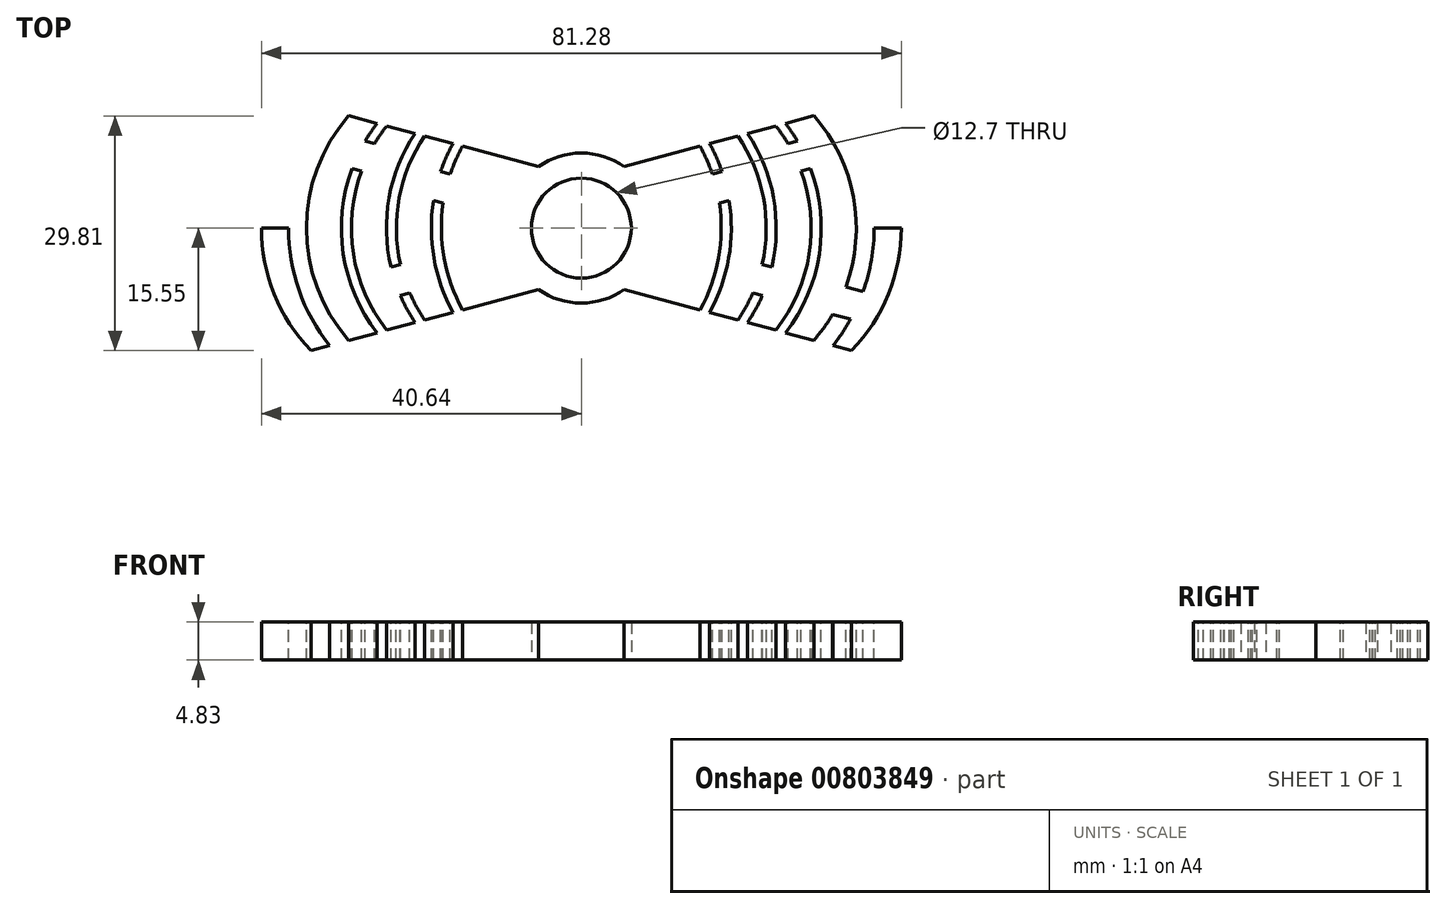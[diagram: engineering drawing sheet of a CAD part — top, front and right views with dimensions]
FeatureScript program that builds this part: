
annotation { "Feature Type Name" : "Feature", "Feature Type Description" : "" }
export const myFeature = defineFeature(function(context is Context, id is Id, definition is map)
    precondition{}
    {
        {
            var Q0;
            Q0=qCreatedBy(makeId("Top.planeOp"),FACE);
            var sketch = newSketch(context, id + "F0", { "sketchPlane" : qUnion([Q0])});
            skCircle(sketch, "E0", {"center": v(0, 0) * mm, "radius": 6.35 * mm});
            skCircle(sketch, "E1", {"center": v(0, 0) * mm, "radius": 9.53 * mm});
            skLineSegment(sketch, "E2", {"start": v(0, 0) * mm, "end": v(40.64, 0) * mm});
            skLineSegment(sketch, "E3", {"start": v(0, 0) * mm, "end": v(-40.64, 0) * mm});
            skLineSegment(sketch, "E4", {"start": v(0, 6.35) * mm, "end": v(34.35, 15.55) * mm});
            skLineSegment(sketch, "E5", {"start": v(0, -6.35) * mm, "end": v(34.35, -15.55) * mm});
            skLineSegment(sketch, "E6", {"start": v(0, -6.35) * mm, "end": v(-34.35, -15.55) * mm});
            skLineSegment(sketch, "E7", {"start": v(0, 6.35) * mm, "end": v(-34.35, 15.55) * mm});
            skArc(sketch, "E8", {"start": v(34.35, -15.55) * mm, "mid": v(40.64, 0) * mm, "end": v(34.35, 15.55) * mm});
            skArc(sketch, "E9", {"start": v(-34.35, 15.55) * mm, "mid": v(-40.64, 0) * mm, "end": v(-34.35, -15.55) * mm});
            skSolve(sketch);
        }
        {
            var Q0;
            Q0=qSketchRegion(id+"F0",true);
            extrude(context, id + "F1", {"entities" : qUnion([Q0]), "depth" : 4.83 * mm, "offsetDistance" : 25.4 * mm});
        }
        {
            var Q0;
            Q0=makeQuery(id+"F1.opExtrude","CAP_FACE",FACE,{"disambiguationData":[OSD([sQuery(id+"F0.wireOp",EDGE,"E0"),sQuery(id+"F0.wireOp",EDGE,"E1"),sQuery(id+"F0.wireOp",EDGE,"E4"),sQuery(id+"F0.wireOp",EDGE,"E5"),sQuery(id+"F0.wireOp",EDGE,"E6"),sQuery(id+"F0.wireOp",EDGE,"E7"),sQuery(id+"F0.wireOp",EDGE,"E8"),sQuery(id+"F0.wireOp",EDGE,"E9")])],"isStart":false});
            var sketch = newSketch(context, id + "F2", { "sketchPlane" : qUnion([Q0])});
            skLineSegment(sketch, "E10", {"start": v(-6.35, 0) * mm, "end": v(-40.64, 0) * mm});
            skLineSegment(sketch, "E11", {"start": v(-5.45, -7.81) * mm, "end": v(-34.35, -15.55) * mm});
            skLineSegment(sketch, "E12", {"start": v(-34.35, 15.55) * mm, "end": v(-5.45, 7.81) * mm});
            skArc(sketch, "E13", {"start": v(-34.35, 15.55) * mm, "mid": v(-40.64, 0) * mm, "end": v(-34.35, -15.55) * mm});
            skLineSegment(sketch, "E14", {"start": v(5.45, -7.81) * mm, "end": v(34.35, -15.55) * mm});
            skLineSegment(sketch, "E15", {"start": v(6.35, 0) * mm, "end": v(40.64, 0) * mm});
            skLineSegment(sketch, "E16", {"start": v(5.45, 7.81) * mm, "end": v(34.35, 15.55) * mm});
            skLineSegment(sketch, "E17", {"start": v(-34.93, 0) * mm, "end": v(-34.93, 2.66) * mm});
            skLineSegment(sketch, "E18", {"start": v(-29.21, 0) * mm, "end": v(-29.21, 2.66) * mm});
            skLineSegment(sketch, "E19", {"start": v(-23.5, 0) * mm, "end": v(-23.5, 2.66) * mm});
            skLineSegment(sketch, "E20", {"start": v(-17.78, 0) * mm, "end": v(-17.78, 2.49) * mm});
            skLineSegment(sketch, "E21", {"start": v(-19.9, 11.68) * mm, "end": v(-20.56, 9.23) * mm});
            skLineSegment(sketch, "E22", {"start": v(-24.72, 12.97) * mm, "end": v(-25.37, 10.52) * mm});
            skLineSegment(sketch, "E23", {"start": v(-29.53, 14.26) * mm, "end": v(-30.19, 11.8) * mm});
            skLineSegment(sketch, "E24", {"start": v(-15.08, 10.4) * mm, "end": v(-15.74, 7.94) * mm});
            skLineSegment(sketch, "E25.MirrorCS", {"start": v(-29.53, -14.26) * mm, "end": v(-30.19, -11.8) * mm});
            skLineSegment(sketch, "E26.MirrorCS", {"start": v(-24.72, -12.97) * mm, "end": v(-25.37, -10.52) * mm});
            skLineSegment(sketch, "E27.MirrorCS", {"start": v(-19.9, -11.68) * mm, "end": v(-20.56, -9.23) * mm});
            skLineSegment(sketch, "E28.MirrorCS", {"start": v(-15.08, -10.4) * mm, "end": v(-15.74, -7.94) * mm});
            skArc(sketch, "E29", {"start": v(-29.53, 14.26) * mm, "mid": v(-34.93, 0) * mm, "end": v(-29.53, -14.26) * mm});
            skArc(sketch, "E30", {"start": v(-24.72, 12.97) * mm, "mid": v(-29.21, 0) * mm, "end": v(-24.72, -12.97) * mm});
            skArc(sketch, "E31", {"start": v(-19.9, 11.68) * mm, "mid": v(-23.5, 0) * mm, "end": v(-19.9, -11.68) * mm});
            skArc(sketch, "E32", {"start": v(-15.08, 10.4) * mm, "mid": v(-17.78, 0) * mm, "end": v(-15.08, -10.4) * mm});
            skArc(sketch, "E33", {"start": v(-31.99, 14.92) * mm, "mid": v(-37.2, 0) * mm, "end": v(-31.99, -14.92) * mm});
            skArc(sketch, "E34", {"start": v(-25.94, 13.3) * mm, "mid": v(-30.48, 0) * mm, "end": v(-25.94, -13.3) * mm});
            skArc(sketch, "E35", {"start": v(-21.13, 12.01) * mm, "mid": v(-24.76, 0) * mm, "end": v(-21.13, -12.01) * mm});
            skArc(sketch, "E36", {"start": v(-16.31, 10.72) * mm, "mid": v(-19.05, 0) * mm, "end": v(-16.31, -10.72) * mm});
            skLineSegment(sketch, "E37", {"start": v(-34.22, -11.57) * mm, "end": v(-31.93, -10.96) * mm});
            skLineSegment(sketch, "E38", {"start": v(-35.8, -8.05) * mm, "end": v(-33.6, -7.46) * mm});
            skLineSegment(sketch, "E39", {"start": v(-21.79, -8.24) * mm, "end": v(-23, -8.57) * mm});
            skLineSegment(sketch, "E40", {"start": v(-22.98, -4.62) * mm, "end": v(-24.2, -4.94) * mm});
            skLineSegment(sketch, "E41", {"start": v(-27.45, 11.08) * mm, "end": v(-26.24, 10.75) * mm});
            skLineSegment(sketch, "E42", {"start": v(-29.12, 7.58) * mm, "end": v(-27.91, 7.26) * mm});
            skLineSegment(sketch, "E43", {"start": v(-17.86, 7.2) * mm, "end": v(-16.65, 6.87) * mm});
            skLineSegment(sketch, "E44", {"start": v(-17.54, 3.16) * mm, "end": v(-18.78, 3.5) * mm});
            skLineSegment(sketch, "E45.MirrorCS", {"start": v(34.35, 15.55) * mm, "end": v(5.45, 7.81) * mm});
            skArc(sketch, "E46.MirrorCS", {"start": v(-21.13, 12.01) * mm, "mid": v(-24.77, 0) * mm, "end": v(-21.13, -12.01) * mm});
            skLineSegment(sketch, "E47.MirrorCS", {"start": v(-5.45, 7.81) * mm, "end": v(-34.35, 15.55) * mm});
            skArc(sketch, "E48.MirrorCS", {"start": v(-34.35, -15.55) * mm, "mid": v(-40.64, 0) * mm, "end": v(-34.35, 15.55) * mm});
            skLineSegment(sketch, "E49.MirrorCS", {"start": v(15.08, 10.4) * mm, "end": v(15.74, 7.94) * mm});
            skLineSegment(sketch, "E50.MirrorCS", {"start": v(15.08, -10.4) * mm, "end": v(15.74, -7.94) * mm});
            skLineSegment(sketch, "E51.MirrorCS", {"start": v(29.21, 0) * mm, "end": v(29.21, 2.66) * mm});
            skLineSegment(sketch, "E52.MirrorCS", {"start": v(24.72, -12.97) * mm, "end": v(25.37, -10.52) * mm});
            skLineSegment(sketch, "E53.MirrorCS", {"start": v(19.9, 11.68) * mm, "end": v(20.56, 9.23) * mm});
            skLineSegment(sketch, "E54.MirrorCS", {"start": v(34.93, 0) * mm, "end": v(34.93, 2.66) * mm});
            skLineSegment(sketch, "E55.MirrorCS", {"start": v(23.5, 0) * mm, "end": v(23.5, 2.66) * mm});
            skLineSegment(sketch, "E56.MirrorCS", {"start": v(19.9, -11.68) * mm, "end": v(20.56, -9.23) * mm});
            skLineSegment(sketch, "E57.MirrorCS", {"start": v(17.78, 0) * mm, "end": v(17.78, 2.49) * mm});
            skLineSegment(sketch, "E58.MirrorCS", {"start": v(24.72, 12.97) * mm, "end": v(25.37, 10.52) * mm});
            skLineSegment(sketch, "E59.MirrorCS", {"start": v(29.53, 14.26) * mm, "end": v(30.19, 11.8) * mm});
            skLineSegment(sketch, "E60.MirrorCS", {"start": v(29.53, -14.26) * mm, "end": v(30.19, -11.8) * mm});
            skLineSegment(sketch, "E61.MirrorCS", {"start": v(17.54, 3.16) * mm, "end": v(18.78, 3.5) * mm});
            skLineSegment(sketch, "E62.MirrorCS", {"start": v(17.86, 7.2) * mm, "end": v(16.65, 6.87) * mm});
            skLineSegment(sketch, "E63.MirrorCS", {"start": v(22.98, -4.62) * mm, "end": v(24.2, -4.94) * mm});
            skLineSegment(sketch, "E64.MirrorCS", {"start": v(21.79, -8.24) * mm, "end": v(23, -8.57) * mm});
            skLineSegment(sketch, "E65.MirrorCS", {"start": v(29.12, 7.58) * mm, "end": v(27.91, 7.26) * mm});
            skLineSegment(sketch, "E66.MirrorCS", {"start": v(34.22, -11.57) * mm, "end": v(31.93, -10.96) * mm});
            skLineSegment(sketch, "E67.MirrorCS", {"start": v(35.8, -8.05) * mm, "end": v(33.6, -7.46) * mm});
            skLineSegment(sketch, "E68.MirrorCS", {"start": v(27.45, 11.08) * mm, "end": v(26.24, 10.75) * mm});
            skArc(sketch, "E69.MirrorCS", {"start": v(24.72, 12.97) * mm, "mid": v(29.21, 0) * mm, "end": v(24.72, -12.97) * mm});
            skArc(sketch, "E70.MirrorCS", {"start": v(19.9, 11.68) * mm, "mid": v(23.5, 0) * mm, "end": v(19.9, -11.68) * mm});
            skArc(sketch, "E71.MirrorCS", {"start": v(15.08, 10.4) * mm, "mid": v(17.78, 0) * mm, "end": v(15.08, -10.4) * mm});
            skArc(sketch, "E72.MirrorCS", {"start": v(29.53, 14.26) * mm, "mid": v(34.93, 0) * mm, "end": v(29.53, -14.26) * mm});
            skArc(sketch, "E73.MirrorCS", {"start": v(25.94, 13.3) * mm, "mid": v(30.48, 0) * mm, "end": v(25.94, -13.3) * mm});
            skArc(sketch, "E74.MirrorCS", {"start": v(21.13, 12.01) * mm, "mid": v(24.76, 0) * mm, "end": v(21.13, -12.01) * mm});
            skArc(sketch, "E75.MirrorCS", {"start": v(31.99, 14.92) * mm, "mid": v(37.2, 0) * mm, "end": v(31.99, -14.92) * mm});
            skArc(sketch, "E76.MirrorCS", {"start": v(16.31, 10.72) * mm, "mid": v(19.05, 0) * mm, "end": v(16.31, -10.72) * mm});
            skArc(sketch, "E77.MirrorCS", {"start": v(34.35, 15.55) * mm, "mid": v(40.64, 0) * mm, "end": v(34.35, -15.55) * mm});
            skArc(sketch, "E78.MirrorCS", {"start": v(21.13, 12.01) * mm, "mid": v(24.77, 0) * mm, "end": v(21.13, -12.01) * mm});
            skArc(sketch, "E79.MirrorCS", {"start": v(34.35, -15.55) * mm, "mid": v(40.64, 0) * mm, "end": v(34.35, 15.55) * mm});
            skSolve(sketch);
        }
        {
            var Q0;
            {var subQ0=sQuery(id+"F2.wireOp",EDGE,"E38");Q0=makeQuery(id+"F2.imprint","IMPRINT",FACE,{"disambiguationData":[TD([[makeQuery(id+"F2.imprint","IMPRINT",EDGE,{"derivedFrom":subQ0}),1.0]])]});}
            var Q1;
            {var subQ0=sQuery(id+"F2.wireOp",EDGE,"E47.MirrorCS");var subQ1=sQuery(id+"F2.wireOp",EDGE,"E33");var subQ2=makeQuery(id+"F2.imprint","INTERSECT",VERTEX,{"derivedFrom":[subQ1,subQ0]});Q1=makeQuery(id+"F2.imprint","IMPRINT",FACE,{"disambiguationData":[TD([[makeQuery(id+"F2.imprint","IMPRINT",EDGE,{"disambiguationData":[TD([[subQ2,-1.0]])],"derivedFrom":subQ1}),1.0]])]});}
            var Q2;
            {var subQ0=sQuery(id+"F2.wireOp",EDGE,"E37");Q2=makeQuery(id+"F2.imprint","IMPRINT",FACE,{"disambiguationData":[TD([[makeQuery(id+"F2.imprint","IMPRINT",EDGE,{"derivedFrom":subQ0}),-1.0]])]});}
            var Q3;
            {var subQ0=sQuery(id+"F2.wireOp",EDGE,"E30");var subQ1=sQuery(id+"F2.wireOp",EDGE,"E10");var subQ2=makeQuery(id+"F2.imprint","INTERSECT",VERTEX,{"derivedFrom":[subQ1,subQ0]});Q3=makeQuery(id+"F2.imprint","IMPRINT",FACE,{"disambiguationData":[TD([[makeQuery(id+"F2.imprint","IMPRINT",EDGE,{"disambiguationData":[TD([[subQ2,-1.0]])],"derivedFrom":subQ1}),1.0]])]});}
            var Q4;
            {var subQ0=sQuery(id+"F2.wireOp",EDGE,"E41");Q4=makeQuery(id+"F2.imprint","IMPRINT",FACE,{"disambiguationData":[TD([[makeQuery(id+"F2.imprint","IMPRINT",EDGE,{"derivedFrom":subQ0}),1.0]])]});}
            var Q5;
            {var subQ0=sQuery(id+"F2.wireOp",EDGE,"E42");Q5=makeQuery(id+"F2.imprint","IMPRINT",FACE,{"disambiguationData":[TD([[makeQuery(id+"F2.imprint","IMPRINT",EDGE,{"derivedFrom":subQ0}),-1.0]])]});}
            var Q6;
            {var subQ0=sQuery(id+"F2.wireOp",EDGE,"E31");var subQ1=sQuery(id+"F2.wireOp",EDGE,"E10");var subQ2=makeQuery(id+"F2.imprint","INTERSECT",VERTEX,{"derivedFrom":[subQ1,subQ0]});Q6=makeQuery(id+"F2.imprint","IMPRINT",FACE,{"disambiguationData":[TD([[makeQuery(id+"F2.imprint","IMPRINT",EDGE,{"disambiguationData":[TD([[subQ2,-1.0]])],"derivedFrom":subQ1}),-1.0]])]});}
            var Q7;
            {var subQ0=sQuery(id+"F2.wireOp",EDGE,"E40");Q7=makeQuery(id+"F2.imprint","IMPRINT",FACE,{"disambiguationData":[TD([[makeQuery(id+"F2.imprint","IMPRINT",EDGE,{"derivedFrom":subQ0}),-1.0]])]});}
            var Q8;
            {var subQ0=sQuery(id+"F2.wireOp",EDGE,"E39");Q8=makeQuery(id+"F2.imprint","IMPRINT",FACE,{"disambiguationData":[TD([[makeQuery(id+"F2.imprint","IMPRINT",EDGE,{"derivedFrom":subQ0}),1.0]])]});}
            var Q9;
            {var subQ0=sQuery(id+"F2.wireOp",EDGE,"E32");var subQ1=sQuery(id+"F2.wireOp",EDGE,"E10");var subQ2=makeQuery(id+"F2.imprint","INTERSECT",VERTEX,{"derivedFrom":[subQ1,subQ0]});Q9=makeQuery(id+"F2.imprint","IMPRINT",FACE,{"disambiguationData":[TD([[makeQuery(id+"F2.imprint","IMPRINT",EDGE,{"disambiguationData":[TD([[subQ2,-1.0]])],"derivedFrom":subQ1}),1.0]])]});}
            var Q10;
            {var subQ0=sQuery(id+"F2.wireOp",EDGE,"E44");Q10=makeQuery(id+"F2.imprint","IMPRINT",FACE,{"disambiguationData":[TD([[makeQuery(id+"F2.imprint","IMPRINT",EDGE,{"derivedFrom":subQ0}),1.0]])]});}
            var Q11;
            {var subQ0=sQuery(id+"F2.wireOp",EDGE,"E43");Q11=makeQuery(id+"F2.imprint","IMPRINT",FACE,{"disambiguationData":[TD([[makeQuery(id+"F2.imprint","IMPRINT",EDGE,{"derivedFrom":subQ0}),1.0]])]});}
            var Q12;
            {var subQ0=sQuery(id+"F2.wireOp",EDGE,"E71.MirrorCS");var subQ1=sQuery(id+"F2.wireOp",EDGE,"E15");var subQ2=makeQuery(id+"F2.imprint","INTERSECT",VERTEX,{"derivedFrom":[subQ1,subQ0]});Q12=makeQuery(id+"F2.imprint","IMPRINT",FACE,{"disambiguationData":[TD([[makeQuery(id+"F2.imprint","IMPRINT",EDGE,{"disambiguationData":[TD([[subQ2,-1.0]])],"derivedFrom":subQ1}),-1.0]])]});}
            var Q13;
            {var subQ5=sQuery(id+"F2.wireOp",EDGE,"E61.MirrorCS");Q13=makeQuery(id+"F2.imprint","IMPRINT",FACE,{"disambiguationData":[TD([[makeQuery(id+"F2.imprint","IMPRINT",EDGE,{"derivedFrom":subQ5}),-1.0]])]});}
            var Q14;
            {var subQ5=sQuery(id+"F2.wireOp",EDGE,"E62.MirrorCS");Q14=makeQuery(id+"F2.imprint","IMPRINT",FACE,{"disambiguationData":[TD([[makeQuery(id+"F2.imprint","IMPRINT",EDGE,{"derivedFrom":subQ5}),-1.0]])]});}
            var Q15;
            {var subQ0=sQuery(id+"F2.wireOp",EDGE,"E70.MirrorCS");var subQ1=sQuery(id+"F2.wireOp",EDGE,"E15");var subQ2=makeQuery(id+"F2.imprint","INTERSECT",VERTEX,{"derivedFrom":[subQ1,subQ0]});Q15=makeQuery(id+"F2.imprint","IMPRINT",FACE,{"disambiguationData":[TD([[makeQuery(id+"F2.imprint","IMPRINT",EDGE,{"disambiguationData":[TD([[subQ2,-1.0]])],"derivedFrom":subQ1}),1.0]])]});}
            var Q16;
            {var subQ5=sQuery(id+"F2.wireOp",EDGE,"E63.MirrorCS");Q16=makeQuery(id+"F2.imprint","IMPRINT",FACE,{"disambiguationData":[TD([[makeQuery(id+"F2.imprint","IMPRINT",EDGE,{"derivedFrom":subQ5}),1.0]])]});}
            var Q17;
            {var subQ5=sQuery(id+"F2.wireOp",EDGE,"E64.MirrorCS");Q17=makeQuery(id+"F2.imprint","IMPRINT",FACE,{"disambiguationData":[TD([[makeQuery(id+"F2.imprint","IMPRINT",EDGE,{"derivedFrom":subQ5}),-1.0]])]});}
            var Q18;
            {var subQ0=sQuery(id+"F2.wireOp",EDGE,"E69.MirrorCS");var subQ1=sQuery(id+"F2.wireOp",EDGE,"E15");var subQ2=makeQuery(id+"F2.imprint","INTERSECT",VERTEX,{"derivedFrom":[subQ1,subQ0]});Q18=makeQuery(id+"F2.imprint","IMPRINT",FACE,{"disambiguationData":[TD([[makeQuery(id+"F2.imprint","IMPRINT",EDGE,{"disambiguationData":[TD([[subQ2,-1.0]])],"derivedFrom":subQ1}),-1.0]])]});}
            var Q19;
            {var subQ5=sQuery(id+"F2.wireOp",EDGE,"E65.MirrorCS");Q19=makeQuery(id+"F2.imprint","IMPRINT",FACE,{"disambiguationData":[TD([[makeQuery(id+"F2.imprint","IMPRINT",EDGE,{"derivedFrom":subQ5}),1.0]])]});}
            var Q20;
            {var subQ5=sQuery(id+"F2.wireOp",EDGE,"E68.MirrorCS");Q20=makeQuery(id+"F2.imprint","IMPRINT",FACE,{"disambiguationData":[TD([[makeQuery(id+"F2.imprint","IMPRINT",EDGE,{"derivedFrom":subQ5}),-1.0]])]});}
            var Q21;
            {var subQ0=sQuery(id+"F2.wireOp",EDGE,"E72.MirrorCS");var subQ1=sQuery(id+"F2.wireOp",EDGE,"E15");var subQ2=makeQuery(id+"F2.imprint","INTERSECT",VERTEX,{"derivedFrom":[subQ1,subQ0]});Q21=makeQuery(id+"F2.imprint","IMPRINT",FACE,{"disambiguationData":[TD([[makeQuery(id+"F2.imprint","IMPRINT",EDGE,{"disambiguationData":[TD([[subQ2,-1.0]])],"derivedFrom":subQ1}),1.0]])]});}
            var Q22;
            {var subQ5=sQuery(id+"F2.wireOp",EDGE,"E67.MirrorCS");Q22=makeQuery(id+"F2.imprint","IMPRINT",FACE,{"disambiguationData":[TD([[makeQuery(id+"F2.imprint","IMPRINT",EDGE,{"derivedFrom":subQ5}),-1.0]])]});}
            var Q23;
            {var subQ5=sQuery(id+"F2.wireOp",EDGE,"E66.MirrorCS");Q23=makeQuery(id+"F2.imprint","IMPRINT",FACE,{"disambiguationData":[TD([[makeQuery(id+"F2.imprint","IMPRINT",EDGE,{"derivedFrom":subQ5}),1.0]])]});}
            extrude(context, id + "F3", {"entities" : qUnion([Q0, Q1, Q2, Q3, Q4, Q5, Q6, Q7, Q8, Q9, Q10, Q11, Q12, Q13, Q14, Q15, Q16, Q17, Q18, Q19, Q20, Q21, Q22, Q23]), "operationType" : NewBodyOperationType.REMOVE, "oppositeDirection" : true, "depth" : 25.4 * mm, "offsetDistance" : 25.4 * mm});
        }
    });
